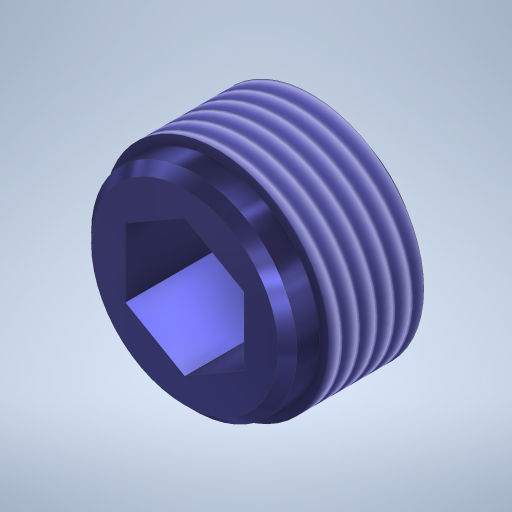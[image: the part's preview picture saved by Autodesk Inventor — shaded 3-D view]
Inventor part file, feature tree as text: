
AUTODESK INVENTOR PART (.ipt)
format: ipt  version: 2023.1 (Build 271208000, 208)  size: 359,936 bytes
history: native  units: in
note: dims shown in document units (in); Inventor stores cm internally (conversion verified against a paired STEP export)
features: extrude x4, sketch x4, chamfer x1, thread x1
ambient origin geometry x8: Origin, YZ Plane, XZ Plane, XY Plane, X Axis, Y Axis, Z Axis, Center Point
bodies: Solid1 (feature_tree)
feature tree (10):
  extrude  "Extrusion1"  Depth=0.2in TaperAngle=0.0deg
  extrude  "Extrusion2"  Depth=0.025in
  extrude  "Extrusion3"  Depth=0.05in TaperAngle=0.0deg
  chamfer  "Chamfer1"  Distance=0.015in Angle=45.0deg
  extrude  "Extrusion4"  Depth=0.05in TaperAngle=0.0deg
  thread  "Thread1"  [1 undecoded]
  sketch  "Sketch1"  dims[d0=0.355in d1=0.2in d2=0.0in]
  sketch  "Sketch2"  dims[d3=0.3in d4=0.025in d5=-0.1031in]
  sketch  "Sketch3"  dims[d6=0.325in d7=0.05in d8=0.0in d9=0.015in d10=0.125in d11=45.0deg]
  sketch  "Sketch4"  dims[d12=0.1875in d13=0.05in d14=0.0in d15=1.0in d16=0.0in]
note: 1 required parameter value undecoded (feature->parameter linkage not recoverable at this tier; creation-order binding heuristic only, values carry confidence <= 0.55)
